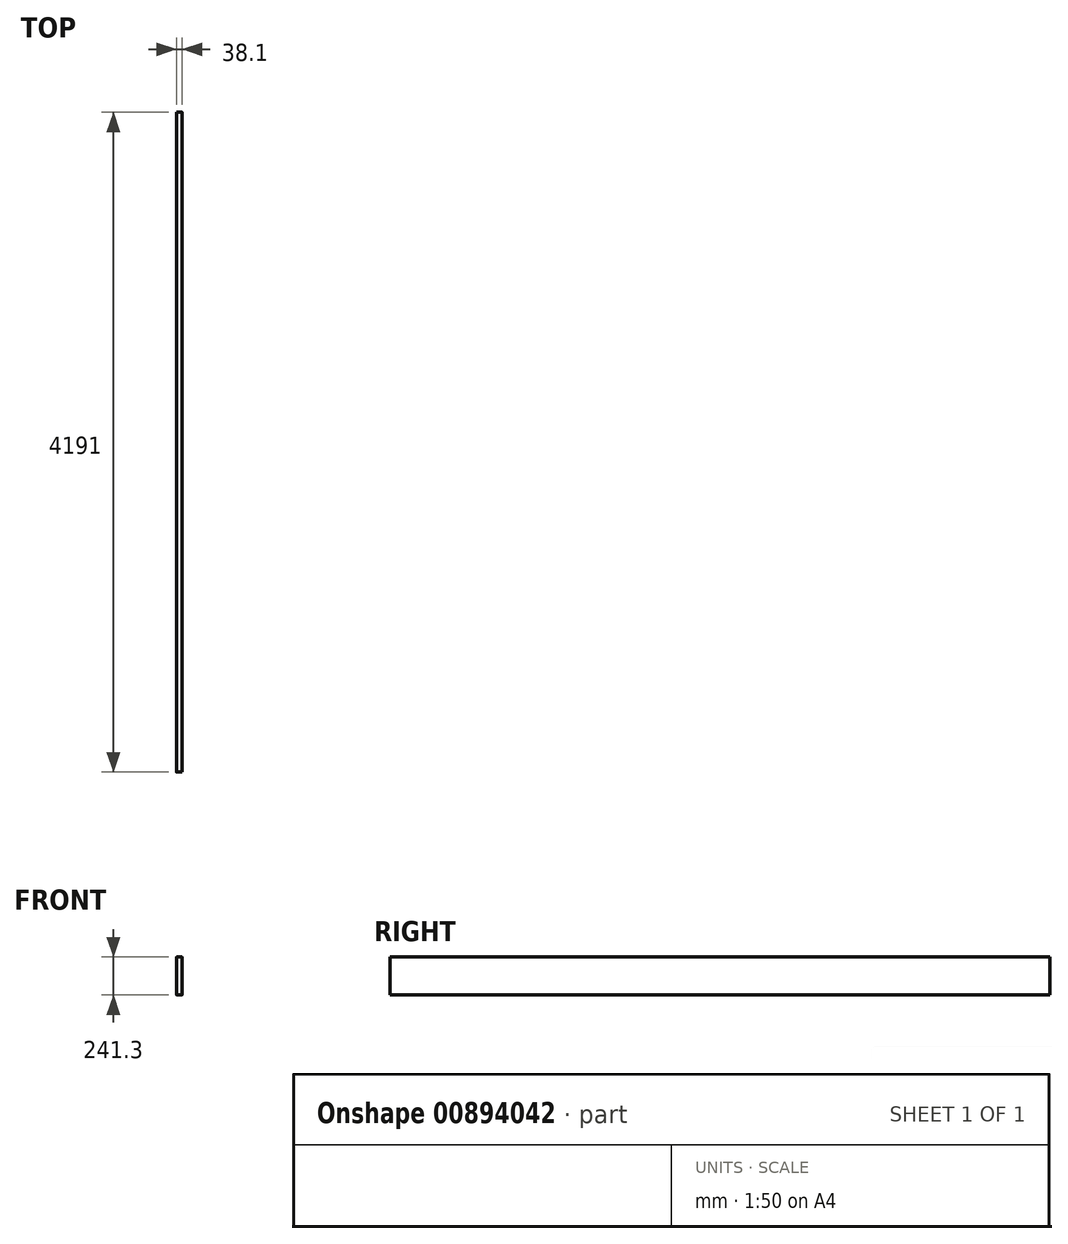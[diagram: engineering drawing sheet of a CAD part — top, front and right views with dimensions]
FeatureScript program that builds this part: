
annotation { "Feature Type Name" : "Feature", "Feature Type Description" : "" }
export const myFeature = defineFeature(function(context is Context, id is Id, definition is map)
    precondition{}
    {
        {
            var Q0;
            Q0=qCreatedBy(makeId("Front.planeOp"),FACE);
            var sketch = newSketch(context, id + "F0", { "sketchPlane" : qUnion([Q0])});
            skLineSegment(sketch, "E0.bottom", {"start": v(81.64, 246.1) * mm, "end": v(113.39, 246.1) * mm});
            skLineSegment(sketch, "E0.top", {"start": v(81.64, 4.8) * mm, "end": v(113.39, 4.8) * mm});
            skLineSegment(sketch, "E0.left", {"start": v(78.46, 242.93) * mm, "end": v(78.46, 7.98) * mm});
            skLineSegment(sketch, "E0.right", {"start": v(116.56, 242.93) * mm, "end": v(116.56, 7.98) * mm});
            skPoint(sketch, "E1.visualSharp", {"position": v(78.46, 246.1) * mm});
            skArc(sketch, "E1.filletArc", {"start": v(81.64, 246.1) * mm, "mid": v(79.4, 245.17) * mm, "end": v(78.46, 242.93) * mm});
            skPoint(sketch, "E2.visualSharp", {"position": v(116.56, 246.1) * mm});
            skArc(sketch, "E2.filletArc", {"start": v(116.56, 242.93) * mm, "mid": v(115.63, 245.17) * mm, "end": v(113.39, 246.1) * mm});
            skPoint(sketch, "E3.visualSharp", {"position": v(116.56, 4.8) * mm});
            skArc(sketch, "E3.filletArc", {"start": v(113.39, 4.8) * mm, "mid": v(115.63, 5.73) * mm, "end": v(116.56, 7.98) * mm});
            skPoint(sketch, "E4.visualSharp", {"position": v(78.46, 4.8) * mm});
            skArc(sketch, "E4.filletArc", {"start": v(78.46, 7.98) * mm, "mid": v(79.4, 5.73) * mm, "end": v(81.64, 4.8) * mm});
            skSolve(sketch);
        }
        {
            var Q0;
            Q0=makeQuery(id+"F0.imprint","IMPRINT",FACE,{"disambiguationData":[TD([[makeQuery(id+"F0.imprint","IMPRINT",EDGE,{"derivedFrom":sQuery(id+"F0.wireOp",EDGE,"E0.bottom")}),-1.0]])]});
            extrude(context, id + "F1", {"entities" : qUnion([Q0]), "depth" : 4191 * mm, "offsetDistance" : 25.4 * mm});
        }
    });
